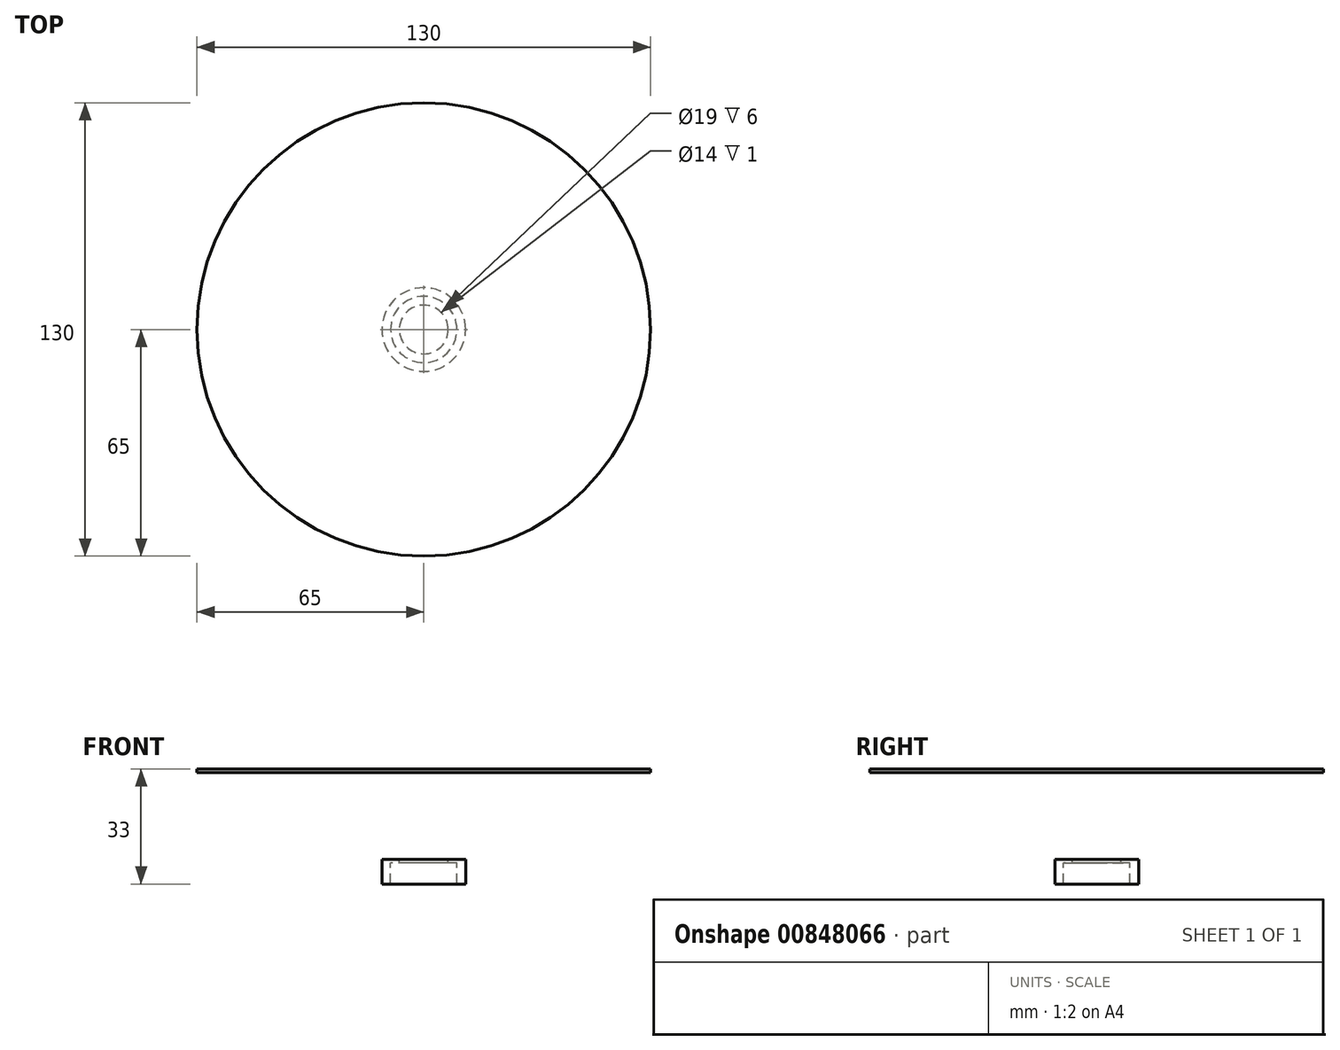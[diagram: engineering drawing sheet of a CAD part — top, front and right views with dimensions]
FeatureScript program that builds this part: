
annotation { "Feature Type Name" : "Feature", "Feature Type Description" : "" }
export const myFeature = defineFeature(function(context is Context, id is Id, definition is map)
    precondition{}
    {
        {
            var Q0;
            Q0=qCreatedBy(makeId("Top.planeOp"),FACE);
            var sketch = newSketch(context, id + "F0", { "sketchPlane" : qUnion([Q0])});
            skCircle(sketch, "E0", {"center": v(0, 0) * mm, "radius": 65 * mm});
            skCircle(sketch, "E1", {"center": v(0, 0) * mm, "radius": 4.25 * mm, "construction": true});
            skSolve(sketch);
        }
        {
            var Q0;
            Q0 = qSketchRegion(id + "F0", true);
            extrude(context, id + "F1", {"entities" : qUnion([Q0]), "depth" : 1 * mm, "offsetDistance" : 25 * mm});
        }
        {
            var Q0;
            Q0=qCreatedBy(makeId("Top.planeOp"),FACE);
            cPlane(context, id + "F2", {"entities" : qUnion([Q0]), "cplaneType" : CPlaneType.OFFSET, "offset" : 25 * mm, "oppositeDirection" : true, "width" : 150 * mm, "height" : 150 * mm});
        }
        {
            var Q0;
            Q0=qCreatedBy(id+"F2.planeOp",FACE);
            var sketch = newSketch(context, id + "F3", { "sketchPlane" : qUnion([Q0])});
            skCircle(sketch, "E2", {"center": v(0, 0) * mm, "radius": 12 * mm});
            skCircle(sketch, "E3", {"center": v(0, 0) * mm, "radius": 9.5 * mm});
            skCircle(sketch, "E4", {"center": v(0, 0) * mm, "radius": 7 * mm});
            skSolve(sketch);
        }
        {
            var Q0;
            Q0=makeQuery(id+"F3.imprint","IMPRINT",FACE,{"disambiguationData":[TD([[makeQuery(id+"F3.imprint","IMPRINT",EDGE,{"derivedFrom":sQuery(id+"F3.wireOp",EDGE,"E2")}),1.0]])]});
            extrude(context, id + "F4", {"entities" : qUnion([Q0]), "oppositeDirection" : true, "depth" : 7 * mm, "offsetDistance" : 25 * mm});
        }
        {
            var Q0;
            Q0=makeQuery(id+"F3.imprint","IMPRINT",FACE,{"disambiguationData":[TD([[makeQuery(id+"F3.imprint","IMPRINT",EDGE,{"derivedFrom":sQuery(id+"F3.wireOp",EDGE,"E3")}),1.0]])]});
            extrude(context, id + "F5", {"entities" : qUnion([Q0]), "operationType" : NewBodyOperationType.ADD, "oppositeDirection" : true, "depth" : 1 * mm, "offsetDistance" : 25 * mm});
        }
    });
